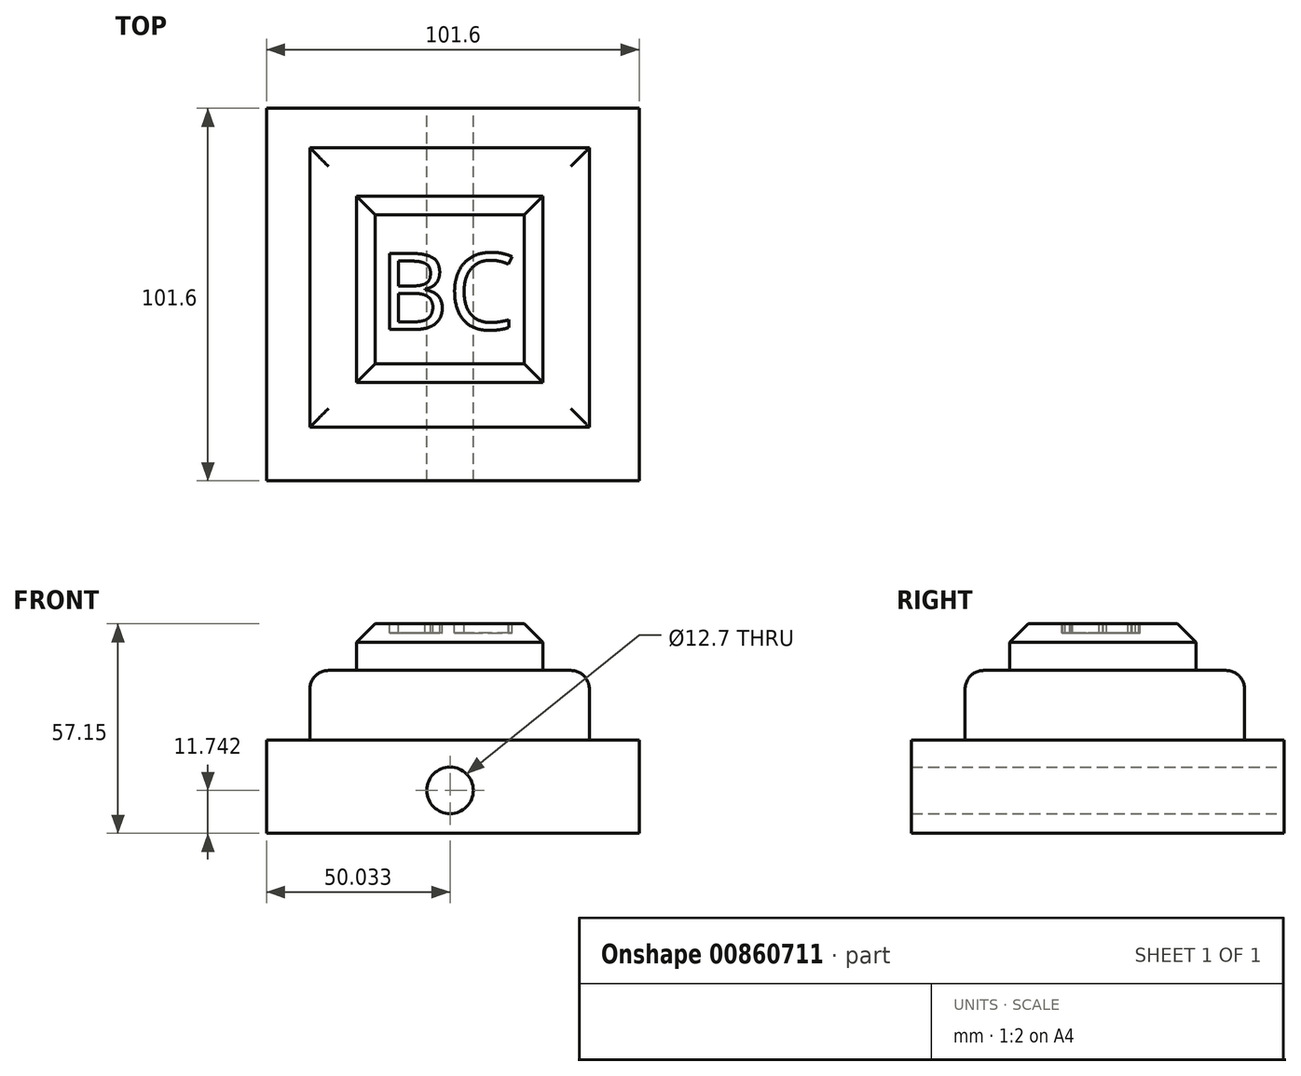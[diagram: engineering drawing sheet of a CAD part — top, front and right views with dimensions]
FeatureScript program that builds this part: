
annotation { "Feature Type Name" : "Feature", "Feature Type Description" : "" }
export const myFeature = defineFeature(function(context is Context, id is Id, definition is map)
    precondition{}
    {
        {
            var Q0;
            Q0=qCreatedBy(makeId("Top.planeOp"),FACE);
            var sketch = newSketch(context, id + "F0", { "sketchPlane" : qUnion([Q0])});
            skLineSegment(sketch, "E0", {"start": v(0, 0) * mm, "end": v(0, 101.6) * mm});
            skLineSegment(sketch, "E1", {"start": v(0, 101.6) * mm, "end": v(101.6, 101.6) * mm});
            skLineSegment(sketch, "E2", {"start": v(101.6, 0) * mm, "end": v(101.6, 101.6) * mm});
            skLineSegment(sketch, "E3", {"start": v(0, 0) * mm, "end": v(101.6, 0) * mm});
            skSolve(sketch);
        }
        {
            var Q0;
            Q0=makeQuery(id+"F0.imprint","IMPRINT",FACE,{"disambiguationData":[TD([[makeQuery(id+"F0.imprint","IMPRINT",EDGE,{"derivedFrom":sQuery(id+"F0.wireOp",EDGE,"E0")}),-1.0]])]});
            extrude(context, id + "F1", {"entities" : qUnion([Q0]), "depth" : 25.4 * mm, "offsetDistance" : 25.4 * mm});
        }
        {
            var Q0;
            Q0=makeQuery(id+"F1.opExtrude","CAP_FACE",FACE,{"disambiguationData":[OSD([sQuery(id+"F0.wireOp",EDGE,"E0"),sQuery(id+"F0.wireOp",EDGE,"E1"),sQuery(id+"F0.wireOp",EDGE,"E2"),sQuery(id+"F0.wireOp",EDGE,"E3")])],"isStart":false});
            var sketch = newSketch(context, id + "F2", { "sketchPlane" : qUnion([Q0])});
            skLineSegment(sketch, "E4", {"start": v(11.83, 90.84) * mm, "end": v(11.83, 14.64) * mm});
            skLineSegment(sketch, "E5", {"start": v(11.83, 14.64) * mm, "end": v(88.03, 14.64) * mm});
            skLineSegment(sketch, "E6", {"start": v(88.03, 14.64) * mm, "end": v(88.03, 90.84) * mm});
            skLineSegment(sketch, "E7", {"start": v(88.03, 90.84) * mm, "end": v(11.83, 90.84) * mm});
            skSolve(sketch);
        }
        {
            var Q0;
            Q0=makeQuery(id+"F2.imprint","IMPRINT",FACE,{"disambiguationData":[TD([[makeQuery(id+"F2.imprint","IMPRINT",EDGE,{"derivedFrom":sQuery(id+"F2.wireOp",EDGE,"E4")}),1.0]])]});
            extrude(context, id + "F3", {"entities" : qUnion([Q0]), "operationType" : NewBodyOperationType.ADD, "depth" : 19.05 * mm, "offsetDistance" : 25.4 * mm});
        }
        {
            var Q0;
            Q0=makeQuery(id+"F3.opExtrude","CAP_FACE",FACE,{"disambiguationData":[OSD([sQuery(id+"F2.wireOp",EDGE,"E4"),sQuery(id+"F2.wireOp",EDGE,"E5"),sQuery(id+"F2.wireOp",EDGE,"E6"),sQuery(id+"F2.wireOp",EDGE,"E7")])],"isStart":false});
            var sketch = newSketch(context, id + "F4", { "sketchPlane" : qUnion([Q0])});
            skLineSegment(sketch, "E8", {"start": v(24.53, 77.6) * mm, "end": v(24.53, 26.8) * mm});
            skLineSegment(sketch, "E9", {"start": v(24.53, 26.8) * mm, "end": v(75.33, 26.8) * mm});
            skLineSegment(sketch, "E10", {"start": v(75.33, 26.8) * mm, "end": v(75.33, 77.6) * mm});
            skLineSegment(sketch, "E11", {"start": v(75.33, 77.6) * mm, "end": v(24.53, 77.6) * mm});
            skSolve(sketch);
        }
        {
            var Q0;
            Q0=makeQuery(id+"F4.imprint","IMPRINT",FACE,{"disambiguationData":[TD([[makeQuery(id+"F4.imprint","IMPRINT",EDGE,{"derivedFrom":sQuery(id+"F4.wireOp",EDGE,"E8")}),1.0]])]});
            extrude(context, id + "F5", {"entities" : qUnion([Q0]), "operationType" : NewBodyOperationType.ADD, "depth" : 12.7 * mm, "offsetDistance" : 25.4 * mm});
        }
        {
            var Q0;
            Q0=makeQuery(id+"F1.opExtrude","SWEPT_FACE",FACE,{"disambiguationData":[OSD([sQuery(id+"F0.wireOp",EDGE,"E1")])]});
            var sketch = newSketch(context, id + "F6", { "sketchPlane" : qUnion([Q0])});
            skCircle(sketch, "E12", {"center": v(-50.03, 11.74) * mm, "radius": 6.35 * mm});
            skSolve(sketch);
        }
        {
            var Q0;
            Q0=makeQuery(id+"F6.imprint","IMPRINT",FACE,{"disambiguationData":[TD([[makeQuery(id+"F6.imprint","IMPRINT",EDGE,{"derivedFrom":sQuery(id+"F6.wireOp",EDGE,"E12")}),1.0]])]});
            extrude(context, id + "F7", {"entities" : qUnion([Q0]), "operationType" : NewBodyOperationType.REMOVE, "oppositeDirection" : true, "depth" : 127 * mm, "offsetDistance" : 25.4 * mm});
        }
        {
            var Q0;
            Q0=makeQuery(id+"F5.opExtrude","CAP_FACE",FACE,{"disambiguationData":[OSD([sQuery(id+"F4.wireOp",EDGE,"E8"),sQuery(id+"F4.wireOp",EDGE,"E9"),sQuery(id+"F4.wireOp",EDGE,"E10"),sQuery(id+"F4.wireOp",EDGE,"E11")])],"isStart":false});
            var sketch = newSketch(context, id + "F8", { "sketchPlane" : qUnion([Q0])});
            skText(sketch, "E13", { "text": "BC\n", "fontName": "OpenSans-Regular.ttf"});
            const initialGuessF8  = {"E13": [0.03072, 0.04133, 1, 0, 0.02088]};
            skSetInitialGuess(sketch, initialGuessF8);
            skSolve(sketch);
        }
        {
            var Q0;
            Q0 = qSketchRegion(id + "F8", true);
            extrude(context, id + "F9", {"entities" : qUnion([Q0]), "operationType" : NewBodyOperationType.REMOVE, "oppositeDirection" : true, "depth" : 2.54 * mm, "offsetDistance" : 25.4 * mm});
        }
        {
            var Q0;
            Q0=makeQuery(id+"F3.opExtrude","CAP_EDGE",EDGE,{"disambiguationData":[OSD([sQuery(id+"F2.wireOp",EDGE,"E5")])],"isStart":false});
            var Q1;
            Q1=makeQuery(id+"F3.opExtrude","CAP_EDGE",EDGE,{"disambiguationData":[OSD([sQuery(id+"F2.wireOp",EDGE,"E4")])],"isStart":false});
            var Q2;
            Q2=makeQuery(id+"F3.opExtrude","CAP_EDGE",EDGE,{"disambiguationData":[OSD([sQuery(id+"F2.wireOp",EDGE,"E6")])],"isStart":false});
            var Q3;
            Q3=makeQuery(id+"F3.opExtrude","CAP_EDGE",EDGE,{"disambiguationData":[OSD([sQuery(id+"F2.wireOp",EDGE,"E7")])],"isStart":false});
            fillet(context, id + "F10", {"entities" : qUnion([Q0, Q1, Q2, Q3]), "radius" : 5.08 * mm, "tangentPropagation" : true, "allowEdgeOverflow" : false});
        }
        {
            var Q0;
            Q0=makeQuery(id+"F5.opExtrude","CAP_EDGE",EDGE,{"disambiguationData":[OSD([sQuery(id+"F4.wireOp",EDGE,"E9")])],"isStart":false});
            var Q1;
            Q1=makeQuery(id+"F5.opExtrude","CAP_EDGE",EDGE,{"disambiguationData":[OSD([sQuery(id+"F4.wireOp",EDGE,"E10")])],"isStart":false});
            var Q2;
            Q2=makeQuery(id+"F5.opExtrude","CAP_EDGE",EDGE,{"disambiguationData":[OSD([sQuery(id+"F4.wireOp",EDGE,"E11")])],"isStart":false});
            var Q3;
            Q3=makeQuery(id+"F5.opExtrude","CAP_EDGE",EDGE,{"disambiguationData":[OSD([sQuery(id+"F4.wireOp",EDGE,"E8")])],"isStart":false});
            chamfer(context, id + "F11", {"entities" : qUnion([Q0, Q1, Q2, Q3]), "width" : 5.08 * mm, "tangentPropagation" : true});
        }
    });
